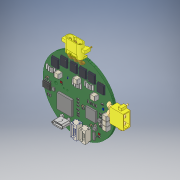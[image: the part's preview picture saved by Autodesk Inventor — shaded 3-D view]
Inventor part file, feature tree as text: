
AUTODESK INVENTOR PART (.ipt)
format: ipt  version: 2019.4 (Build 234330000, 330)  size: 7,352,832 bytes
history: native  units: mm
features: other x220, extrude x91, sketch x1, shell x1
ambient origin geometry x8: Origin, YZ Plane, XZ Plane, XY Plane, X Axis, Y Axis, Z Axis, Center Point
bodies: Solid1 (feature_tree), Solid2 (feature_tree), Solid3 (feature_tree), Solid4 (feature_tree), Solid5 (feature_tree), Solid6 (feature_tree), Solid7 (feature_tree), Solid8 (feature_tree), Solid9 (feature_tree), Solid10 (feature_tree), Solid11 (feature_tree), Solid12 (feature_tree), Solid13 (feature_tree), Solid14 (feature_tree), Solid15 (feature_tree), Solid16 (feature_tree), Solid17 (feature_tree), Solid18 (feature_tree), Solid19 (feature_tree), Solid20 (feature_tree), Solid21 (feature_tree), Solid22 (feature_tree), Solid23 (feature_tree), Solid24 (feature_tree), Solid25 (feature_tree), Solid26 (feature_tree), Solid27 (feature_tree), Solid28 (feature_tree), Solid29 (feature_tree), Solid30 (feature_tree), Solid31 (feature_tree), Solid32 (feature_tree), Solid33 (feature_tree), Solid34 (feature_tree), Solid35 (feature_tree), Solid36 (feature_tree), Solid37 (feature_tree), Solid38 (feature_tree), Solid39 (feature_tree), Solid40 (feature_tree), Solid41 (feature_tree), Solid42 (feature_tree), Solid43 (feature_tree), Solid44 (feature_tree), Solid45 (feature_tree), Solid46 (feature_tree), Solid47 (feature_tree), Solid48 (feature_tree), Solid49 (feature_tree), Solid50 (feature_tree), Solid51 (feature_tree), Solid52 (feature_tree), Solid53 (feature_tree), Solid54 (feature_tree), Solid55 (feature_tree), Solid56 (feature_tree), Solid57 (feature_tree), Solid58 (feature_tree), Solid59 (feature_tree), Solid60 (feature_tree), Solid61 (feature_tree), Solid62 (feature_tree), Solid63 (feature_tree), Solid64 (feature_tree), Solid65 (feature_tree), Solid66 (feature_tree), Solid67 (feature_tree), Solid68 (feature_tree), Solid69 (feature_tree), Solid70 (feature_tree), Solid71 (feature_tree), Solid72 (feature_tree), Solid73 (feature_tree), Solid74 (feature_tree), Solid75 (feature_tree), Solid76 (feature_tree), Solid77 (feature_tree), Solid78 (feature_tree), Solid79 (feature_tree), Solid80 (feature_tree), Solid81 (feature_tree), Solid82 (feature_tree), Solid83 (feature_tree), Solid84 (feature_tree), Solid85 (feature_tree), Solid86 (feature_tree), Solid87 (feature_tree), Solid88 (feature_tree), Solid89 (feature_tree), Solid90 (feature_tree), Solid91 (feature_tree), Solid92 (feature_tree), Solid93 (feature_tree), Solid94 (feature_tree), Solid95 (feature_tree), Solid96 (feature_tree), Solid97 (feature_tree), Solid98 (feature_tree), Solid99 (feature_tree), Solid100 (feature_tree), Solid101 (feature_tree), Solid102 (feature_tree), Solid103 (feature_tree), Solid104 (feature_tree), Solid105 (feature_tree), Solid106 (feature_tree), Solid107 (feature_tree), Solid108 (feature_tree), Solid109 (feature_tree), Solid110 (feature_tree), Solid111 (feature_tree), Solid112 (feature_tree), Solid113 (feature_tree), Solid114 (feature_tree), Solid115 (feature_tree), Solid116 (feature_tree), Solid117 (feature_tree), Solid118 (feature_tree), Solid119 (feature_tree), Solid120 (feature_tree), Solid121 (feature_tree), Solid122 (feature_tree), Solid123 (feature_tree), Solid124 (feature_tree), Solid125 (feature_tree), Solid126 (feature_tree), Solid127 (feature_tree), Solid128 (feature_tree), Solid129 (feature_tree), Solid130 (feature_tree), Solid131 (feature_tree), Solid132 (feature_tree), Solid133 (feature_tree), Solid134 (feature_tree), Solid135 (feature_tree), Solid136 (feature_tree), Solid137 (feature_tree), Solid138 (feature_tree), Solid139 (feature_tree), Solid140 (feature_tree), Solid141 (feature_tree), Solid142 (feature_tree), Solid143 (feature_tree), Solid144 (feature_tree), Solid145 (feature_tree), Solid146 (feature_tree), Solid147 (feature_tree), Solid148 (feature_tree), Solid149 (feature_tree), Solid150 (feature_tree), Solid151 (feature_tree), Solid152 (feature_tree), Solid153 (feature_tree), Solid154 (feature_tree), Solid155 (feature_tree), Solid156 (feature_tree), Solid157 (feature_tree), Solid158 (feature_tree), Solid159 (feature_tree), Solid160 (feature_tree), Solid161 (feature_tree), Solid162 (feature_tree), Solid163 (feature_tree), Solid164 (feature_tree), Solid165 (feature_tree), Solid166 (feature_tree), Solid167 (feature_tree), Solid168 (feature_tree), Solid169 (feature_tree), Solid170 (feature_tree), Solid171 (feature_tree), Solid172 (feature_tree), Solid173 (feature_tree), Solid174 (feature_tree), Solid175 (feature_tree), Solid176 (feature_tree), Solid177 (feature_tree), Solid178 (feature_tree), Solid179 (feature_tree), Solid180 (feature_tree), Solid181 (feature_tree), Solid182 (feature_tree), Solid183 (feature_tree), Solid184 (feature_tree), Solid185 (feature_tree), Solid186 (feature_tree), Solid187 (feature_tree), Solid188 (feature_tree), Solid189 (feature_tree), Solid190 (feature_tree), Solid191 (feature_tree), Solid192 (feature_tree), Solid193 (feature_tree), Solid194 (feature_tree), Solid195 (feature_tree), Solid196 (feature_tree), Solid197 (feature_tree), Solid198 (feature_tree), Solid199 (feature_tree), Solid200 (feature_tree), Solid201 (feature_tree), Solid202 (feature_tree), Solid203 (feature_tree), Solid204 (feature_tree), Solid205 (feature_tree), Solid206 (feature_tree), Solid207 (feature_tree), Solid208 (feature_tree), Solid209 (feature_tree), Solid210 (feature_tree), Solid211 (feature_tree), Solid212 (feature_tree), Solid213 (feature_tree), Solid214 (feature_tree), Solid215 (feature_tree), Solid216 (feature_tree), Solid217 (feature_tree), Solid218 (feature_tree), Solid219 (feature_tree), Solid220 (feature_tree), Solid221 (feature_tree), Solid222 (feature_tree), Solid223 (feature_tree), Solid224 (feature_tree), Solid225 (feature_tree), Solid226 (feature_tree), Solid227 (feature_tree), Solid228 (feature_tree), Solid229 (feature_tree), Solid230 (feature_tree), Solid231 (feature_tree), Solid232 (feature_tree), Solid233 (feature_tree), Solid234 (feature_tree), Solid235 (feature_tree), Solid236 (feature_tree), Solid237 (feature_tree), Solid238 (feature_tree), Solid239 (feature_tree), Solid240 (feature_tree), Solid241 (feature_tree), Solid242 (feature_tree), Solid243 (feature_tree), Solid244 (feature_tree), Solid245 (feature_tree), Solid246 (feature_tree), Solid247 (feature_tree), Solid248 (feature_tree), Solid249 (feature_tree), Solid250 (feature_tree), Solid251 (feature_tree), Solid252 (feature_tree), Solid253 (feature_tree), Solid254 (feature_tree), Solid255 (feature_tree), Solid256 (feature_tree), Solid257 (feature_tree), Solid258 (feature_tree), Solid259 (feature_tree), Solid260 (feature_tree), Solid261 (feature_tree), Solid262 (feature_tree), Solid263 (feature_tree), Solid264 (feature_tree), Solid265 (feature_tree), Solid266 (feature_tree), Solid267 (feature_tree), Solid268 (feature_tree), Solid269 (feature_tree), Solid270 (feature_tree), Solid271 (feature_tree), Solid272 (feature_tree), Solid273 (feature_tree), Solid274 (feature_tree), Solid275 (feature_tree), Solid276 (feature_tree), Solid277 (feature_tree), Solid278 (feature_tree), Solid279 (feature_tree), Solid280 (feature_tree), Solid281 (feature_tree), Solid282 (feature_tree), Solid283 (feature_tree), Solid284 (feature_tree), Solid285 (feature_tree), Solid286 (feature_tree), Solid287 (feature_tree), Solid288 (feature_tree), Solid289 (feature_tree), Solid290 (feature_tree), Solid291 (feature_tree), Solid292 (feature_tree), Solid293 (feature_tree), Solid294 (feature_tree), Solid295 (feature_tree), Solid296 (feature_tree), Solid297 (feature_tree), Solid298 (feature_tree), Solid299 (feature_tree), Solid300 (feature_tree), Solid301 (feature_tree), Solid302 (feature_tree), Solid303 (feature_tree), Solid304 (feature_tree), Solid305 (feature_tree), Solid306 (feature_tree), Solid307 (feature_tree), Solid308 (feature_tree), Solid309 (feature_tree)
feature tree (313):
  extrude  "Extrusion1"  Depth=30.0mm TaperAngle=0.0deg
  sketch  "Sketch1"  dims[d0=50.0mm d1=30.0mm d2=30.0mm d3=0.0mm d4=0.0mm d5=16.000001mm]
  other  "Board_1:1"
  extrude  "Extruded_2:1"  Depth=16.000001mm
  extrude  "Extruded_2:2"  [1 undecoded]
  other  "JST_BM04B-GHS-TBT_7:1"
  other  "0603_resistor_9:1"
  other  "0603_resistor_9:2"
  other  "TER2-2_11:1"
  other  "TER2-1_12:1"
  other  "TER2_13:1"
  other  "TER2-3_14:1"
  other  "TER2-4_15:1"
  other  "HOUSING-1_17:1"
  shell  "SHELL_18:1"  [1 undecoded]
  extrude  "Extruded_21:1"  [1 undecoded]
  extrude  "Extruded_24:1"  [1 undecoded]
  extrude  "Extruded_27:1"  [1 undecoded]
  extrude  "Extruded_29:1"  [1 undecoded]
  extrude  "Extruded_29:2"  [1 undecoded]
  other  "0603_cap_33:1"
  extrude  "Extruded_35:1"  [1 undecoded]
  extrude  "Extruded_37:1"  [1 undecoded]
  extrude  "Extruded_35:2"  [1 undecoded]
  other  "User_Library-DFN5x6_SO8FL_Extruded_41:1"
  other  "User_Library-DFN5x6_SO8FL_Extruded_2_43:1"
  other  "User_Library-DFN5x6_SO8FL_Extruded_2_43:2"
  other  "User_Library-DFN5x6_SO8FL_Extruded_41:2"
  other  "User_Library-DFN5x6_SO8FL_Cylinder_47:1"
  other  "User_Library-DFN5x6_SO8FL_Extruded_3_49:1"
  other  "User_Library-DFN5x6_SO8FL_Extruded_4_51:1"
  other  "User_Library-DFN5x6_SO8FL_Extruded_5_53:1"
  other  "User_Library-DFN5x6_SO8FL_Extruded_5_53:2"
  other  "User_Library-DFN5x6_SO8FL_Extruded_5_53:3"
  other  "User_Library-DFN5x6_SO8FL_Extruded_5_53:4"
  other  "User_Library-DFN5x6_SO8FL_Extruded_6_58:1"
  extrude  "Extruded_63:1"  [1 undecoded]
  other  "0603_resistor_66:1"
  other  "0603_resistor_66:2"
  other  "0603_resistor_68:1"
  other  "0603_resistor_68:2"
  other  "0603_resistor_70:1"
  other  "0603_resistor_70:2"
  other  "0603_resistor_72:1"
  other  "0603_resistor_72:2"
  extrude  "Extruded_74:1"  [1 undecoded]
  extrude  "Extruded_76:1"  [1 undecoded]
  extrude  "Extruded_76:2"  [1 undecoded]
  extrude  "Extruded_80:1"  [1 undecoded]
  extrude  "Extruded_82:1"  [1 undecoded]
  extrude  "Extruded_82:2"  [1 undecoded]
  extrude  "Extruded_82:3"  [1 undecoded]
  extrude  "Extruded_82:4"  [1 undecoded]
  extrude  "Extruded_80:2"  [1 undecoded]
  other  "0603_cap_90:1"
  other  "0603_cap_92:1"
  other  "0603_cap_94:1"
  extrude  "Extruded_82:5"  [1 undecoded]
  extrude  "Extruded_82:6"  [1 undecoded]
  extrude  "Extruded_80:3"  [1 undecoded]
  extrude  "Extruded_100:1"  [1 undecoded]
  extrude  "Extruded_100:2"  [1 undecoded]
  extrude  "Extruded_103:1"  [1 undecoded]
  extrude  "Extruded_100:3"  [1 undecoded]
  extrude  "Extruded_100:4"  [1 undecoded]
  extrude  "Extruded_103:2"  [1 undecoded]
  extrude  "Extruded_100:5"  [1 undecoded]
  extrude  "Extruded_100:6"  [1 undecoded]
  extrude  "Extruded_103:3"  [1 undecoded]
  extrude  "Extruded_80:4"  [1 undecoded]
  extrude  "Extruded_82:7"  [1 undecoded]
  extrude  "Extruded_82:8"  [1 undecoded]
  extrude  "Extruded_80:5"  [1 undecoded]
  extrude  "Extruded_82:9"  [1 undecoded]
  extrude  "Extruded_82:10"  [1 undecoded]
  extrude  "Extruded_80:6"  [1 undecoded]
  extrude  "Extruded_82:11"  [1 undecoded]
  extrude  "Extruded_82:12"  [1 undecoded]
  extrude  "Extruded_80:7"  [1 undecoded]
  extrude  "Extruded_82:13"  [1 undecoded]
  extrude  "Extruded_82:14"  [1 undecoded]
  extrude  "Extruded_80:8"  [1 undecoded]
  extrude  "Extruded_82:15"  [1 undecoded]
  extrude  "Extruded_82:16"  [1 undecoded]
  extrude  "Extruded_80:9"  [1 undecoded]
  extrude  "Extruded_82:17"  [1 undecoded]
  extrude  "Extruded_82:18"  [1 undecoded]
  extrude  "Extruded_138:1"  [1 undecoded]
  extrude  "Extruded_140:1"  [1 undecoded]
  extrude  "Extruded_140:2"  [1 undecoded]
  other  "User_Library-MR30PW-M_144:1"
  extrude  "Extruded_146:1"  [1 undecoded]
  extrude  "Extruded_149:1"  [1 undecoded]
  extrude  "Extruded_152:1"  [1 undecoded]
  other  "User_Library-SOT-223-2_PIN_SOT-223_2_1_155:1"
  other  "User_Library-SOT-223-2_SOT-223_1_156:1"
  other  "User_Library-SOT-223-2_PIN_SOT-223_2_1_157:1"
  other  "User_Library-SOT-223-2_PIN_SOT-223_1_158:1"
  other  "User_Library-SOT-223-2_PIN_SOT-223_2_1_159:1"
  other  "0603_resistor_162:1"
  other  "0603_resistor_162:2"
  other  "0603_resistor_164:1"
  other  "0603_resistor_164:2"
  other  "0603_resistor_166:1"
  other  "0603_resistor_166:2"
  other  "0603_resistor_168:1"
  other  "0603_resistor_168:2"
  other  "0603_resistor_170:1"
  other  "0603_resistor_170:2"
  other  "0603_resistor_172:1"
  other  "0603_resistor_172:2"
  other  "0603_resistor_174:1"
  other  "0603_resistor_174:2"
  other  "0603_resistor_176:1"
  other  "0603_resistor_176:2"
  other  "0603_resistor_178:1"
  other  "0603_resistor_178:2"
  other  "0603_resistor_180:1"
  other  "0603_resistor_180:2"
  extrude  "Extruded_35:3"  [1 undecoded]
  extrude  "Extruded_37:2"  [1 undecoded]
  extrude  "Extruded_35:4"  [1 undecoded]
  other  "0603_resistor_186:1"
  other  "0603_resistor_186:2"
  other  "CSS2H-2512K-2L00F_188:1"
  other  "0603_resistor_190:1"
  other  "0603_resistor_190:2"
  other  "0603_resistor_192:1"
  other  "0603_resistor_192:2"
  other  "0603_resistor_194:1"
  other  "0603_resistor_194:2"
  other  "0603_resistor_196:1"
  other  "0603_resistor_196:2"
  other  "CSS2H-2512K-2L00F_198:1"
  other  "0603_resistor_200:1"
  other  "0603_resistor_200:2"
  other  "0603_resistor_202:1"
  other  "0603_resistor_202:2"
  other  "0603_resistor_204:1"
  other  "0603_resistor_204:2"
  other  "0603_resistor_206:1"
  other  "0603_resistor_206:2"
  other  "0603_resistor_208:1"
  other  "0603_resistor_208:2"
  other  "CSS2H-2512K-2L00F_210:1"
  other  "0402_resistor_212:1"
  other  "0402_resistor_212:2"
  other  "0603_resistor_214:1"
  other  "0603_resistor_214:2"
  other  "0603_resistor_216:1"
  other  "0603_resistor_216:2"
  other  "0603_resistor_218:1"
  other  "0603_resistor_218:2"
  other  "0603_resistor_220:1"
  other  "0603_resistor_220:2"
  other  "0603_resistor_222:1"
  other  "0603_resistor_222:2"
  other  "0603_resistor_224:1"
  other  "0603_resistor_224:2"
  other  "0603_resistor_226:1"
  other  "0603_resistor_226:2"
  other  "0603_resistor_228:1"
  other  "0603_resistor_228:2"
  other  "0603_resistor_230:1"
  other  "0603_resistor_230:2"
  other  "0603_resistor_232:1"
  other  "0603_resistor_232:2"
  other  "User_Library-DFN5x6_SO8FL_Extruded_41:3"
  other  "User_Library-DFN5x6_SO8FL_Extruded_2_43:3"
  other  "User_Library-DFN5x6_SO8FL_Extruded_2_43:4"
  other  "User_Library-DFN5x6_SO8FL_Extruded_41:4"
  other  "User_Library-DFN5x6_SO8FL_Cylinder_47:2"
  other  "User_Library-DFN5x6_SO8FL_Extruded_3_49:2"
  other  "User_Library-DFN5x6_SO8FL_Extruded_4_51:2"
  other  "User_Library-DFN5x6_SO8FL_Extruded_5_53:5"
  other  "User_Library-DFN5x6_SO8FL_Extruded_5_53:6"
  other  "User_Library-DFN5x6_SO8FL_Extruded_5_53:7"
  other  "User_Library-DFN5x6_SO8FL_Extruded_5_53:8"
  other  "User_Library-DFN5x6_SO8FL_Extruded_6_58:2"
  other  "User_Library-DFN5x6_SO8FL_Extruded_41:5"
  other  "User_Library-DFN5x6_SO8FL_Extruded_2_43:5"
  other  "User_Library-DFN5x6_SO8FL_Extruded_2_43:6"
  other  "User_Library-DFN5x6_SO8FL_Extruded_41:6"
  other  "User_Library-DFN5x6_SO8FL_Cylinder_47:3"
  other  "User_Library-DFN5x6_SO8FL_Extruded_3_49:3"
  other  "User_Library-DFN5x6_SO8FL_Extruded_4_51:3"
  other  "User_Library-DFN5x6_SO8FL_Extruded_5_53:9"
  other  "User_Library-DFN5x6_SO8FL_Extruded_5_53:10"
  other  "User_Library-DFN5x6_SO8FL_Extruded_5_53:11"
  other  "User_Library-DFN5x6_SO8FL_Extruded_5_53:12"
  other  "User_Library-DFN5x6_SO8FL_Extruded_6_58:3"
  other  "body_30xx_238:1"
  other  "land_pattern_30xx_239:1"
  other  "land_pattern_30xx_240:1"
  other  "FER_0603_243:1"
  other  "JST_BM05B-GHS-TBT_245:1"
  other  "LED_0603_Base_RED_247:1"
  other  "LED_0603_Base_RED_247:2"
  other  "LED_0603_Lens_RED_248:1"
  extrude  "Extruded_250:1"  [1 undecoded]
  other  "LED_0603_Lens_BLUE_255:1"
  other  "LED_0603_Base_BLUE_256:1"
  other  "LED_0603_Base_BLUE_256:2"
  other  "LED_0603_Lens_GREEN_258:1"
  other  "LED_0603_Base_GREEN_259:1"
  other  "LED_0603_Base_GREEN_259:2"
  other  "LED_0603_Base_RED_261:1"
  other  "LED_0603_Base_RED_261:2"
  other  "LED_0603_Lens_RED_262:1"
  other  "0402_cap_264:1"
  other  "0603_cap_266:1"
  other  "0603_cap_268:1"
  other  "0402_cap_270:1"
  other  "0603_cap_272:1"
  extrude  "Extruded_82:19"  [1 undecoded]
  extrude  "Extruded_82:20"  [1 undecoded]
  extrude  "Extruded_80:10"  [1 undecoded]
  extrude  "Extruded_29:3"  [1 undecoded]
  extrude  "Extruded_29:4"  [1 undecoded]
  extrude  "Extruded_27:2"  [1 undecoded]
  extrude  "Extruded_82:21"  [1 undecoded]
  extrude  "Extruded_82:22"  [1 undecoded]
  extrude  "Extruded_80:11"  [1 undecoded]
  other  "0603_cap_286:1"
  extrude  "Extruded_63:2"  [1 undecoded]
  other  "0603_cap_290:1"
  other  "0603_cap_292:1"
  extrude  "Extruded_294:1"  [1 undecoded]
  extrude  "Extruded_294:2"  [1 undecoded]
  extrude  "Extruded_297:1"  [1 undecoded]
  other  "0603_cap_300:1"
  extrude  "Extruded_294:3"  [1 undecoded]
  extrude  "Extruded_294:4"  [1 undecoded]
  extrude  "Extruded_297:2"  [1 undecoded]
  other  "0603_cap_306:1"
  extrude  "Extruded_29:5"  [1 undecoded]
  extrude  "Extruded_29:6"  [1 undecoded]
  extrude  "Extruded_27:3"  [1 undecoded]
  other  "0603_cap_312:1"
  other  "0603_cap_314:1"
  other  "0603_cap_316:1"
  other  "0603_cap_318:1"
  other  "0603_cap_320:1"
  other  "0603_cap_322:1"
  other  "0603_cap_324:1"
  other  "0603_cap_326:1"
  other  "0603_cap_328:1"
  other  "0603_cap_330:1"
  other  "User_Library-XT30-_curved_332:1"
  other  "User_Library-XT30-_curved_332:2"
  other  "User_Library-XT30-_curved_332:3"
  extrude  "Extruded_80:12"  [1 undecoded]
  extrude  "Extruded_82:23"  [1 undecoded]
  extrude  "Extruded_82:24"  [1 undecoded]
  extrude  "Extruded_100:7"  [1 undecoded]
  extrude  "Extruded_100:8"  [1 undecoded]
  extrude  "Extruded_103:4"  [1 undecoded]
  extrude  "Extruded_342:1"  [1 undecoded]
  other  "BODY_M08A_35_345:1"
  other  "LEAD_M08A_57_346:1"
  other  "LEAD_M08A_57_347:1"
  other  "LEAD_M08A_57_348:1"
  other  "LEAD_M08A_57_349:1"
  other  "LEAD_M08A_57_350:1"
  other  "LEAD_M08A_57_351:1"
  other  "LEAD_M08A_57_352:1"
  other  "LEAD_M08A_57_353:1"
  other  "MANIFOLD_SOLID_BREP_2784_354:1"
  other  "MANIFOLD_SOLID_BREP_2935_355:1"
  other  "MANIFOLD_SOLID_BREP_3086_356:1"
  other  "MANIFOLD_SOLID_BREP_3237_357:1"
  extrude  "Extruded_362:1"  [1 undecoded]
  extrude  "Extruded_365:1"  [1 undecoded]
  extrude  "Extruded_368:1"  [1 undecoded]
  extrude  "Extruded_370:1"  [1 undecoded]
  other  "User_Library-DFN5x6_SO8FL_Extruded_41:7"
  other  "User_Library-DFN5x6_SO8FL_Extruded_2_43:7"
  other  "User_Library-DFN5x6_SO8FL_Extruded_2_43:8"
  other  "User_Library-DFN5x6_SO8FL_Extruded_41:8"
  other  "User_Library-DFN5x6_SO8FL_Cylinder_47:4"
  other  "User_Library-DFN5x6_SO8FL_Extruded_3_49:4"
  other  "User_Library-DFN5x6_SO8FL_Extruded_4_51:4"
  other  "User_Library-DFN5x6_SO8FL_Extruded_5_53:13"
  other  "User_Library-DFN5x6_SO8FL_Extruded_5_53:14"
  other  "User_Library-DFN5x6_SO8FL_Extruded_5_53:15"
  other  "User_Library-DFN5x6_SO8FL_Extruded_5_53:16"
  other  "User_Library-DFN5x6_SO8FL_Extruded_6_58:4"
  other  "User_Library-DFN5x6_SO8FL_Extruded_41:9"
  other  "User_Library-DFN5x6_SO8FL_Extruded_2_43:9"
  other  "User_Library-DFN5x6_SO8FL_Extruded_2_43:10"
  other  "User_Library-DFN5x6_SO8FL_Extruded_41:10"
  other  "User_Library-DFN5x6_SO8FL_Cylinder_47:5"
  other  "User_Library-DFN5x6_SO8FL_Extruded_3_49:5"
  other  "User_Library-DFN5x6_SO8FL_Extruded_4_51:5"
  other  "User_Library-DFN5x6_SO8FL_Extruded_5_53:17"
  other  "User_Library-DFN5x6_SO8FL_Extruded_5_53:18"
  other  "User_Library-DFN5x6_SO8FL_Extruded_5_53:19"
  other  "User_Library-DFN5x6_SO8FL_Extruded_5_53:20"
  other  "User_Library-DFN5x6_SO8FL_Extruded_6_58:5"
  other  "User_Library-DFN5x6_SO8FL_Extruded_41:11"
  other  "User_Library-DFN5x6_SO8FL_Extruded_2_43:11"
  other  "User_Library-DFN5x6_SO8FL_Extruded_2_43:12"
  other  "User_Library-DFN5x6_SO8FL_Extruded_41:12"
  other  "User_Library-DFN5x6_SO8FL_Cylinder_47:6"
  other  "User_Library-DFN5x6_SO8FL_Extruded_3_49:6"
  other  "User_Library-DFN5x6_SO8FL_Extruded_4_51:6"
  other  "User_Library-DFN5x6_SO8FL_Extruded_5_53:21"
  other  "User_Library-DFN5x6_SO8FL_Extruded_5_53:22"
  other  "User_Library-DFN5x6_SO8FL_Extruded_5_53:23"
  other  "User_Library-DFN5x6_SO8FL_Extruded_5_53:24"
  other  "User_Library-DFN5x6_SO8FL_Extruded_6_58:6"
  other  "Composite1"
  other  "Srf1"
note: 90 required parameter values undecoded (feature->parameter linkage not recoverable at this tier; creation-order binding heuristic only, values carry confidence <= 0.55)
